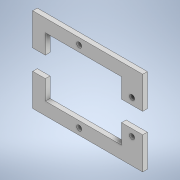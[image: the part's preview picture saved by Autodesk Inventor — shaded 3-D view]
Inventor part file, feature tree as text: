
AUTODESK INVENTOR PART (.ipt)
format: ipt  version: 2022 (Build 260153000, 153)  size: 138,752 bytes
history: native  units: mm
features: other x1, extrude x1, sketch x1
ambient origin geometry x8: Origin, YZ Plane, XZ Plane, XY Plane, X Axis, Y Axis, Z Axis, Center Point
bodies: Body1 (feature_tree)
feature tree (3):
  other  "Sólido1"
  extrude  "Extrusión1"  Depth=5.5mm
  sketch  "Boceto1"  dims[d0=130.0mm d2=100.0mm d4=20.0mm d7=6.0mm d9=12.0mm d10=24.0mm d11=12.0mm d12=24.0mm d13=5.5mm d14=0.0mm]
